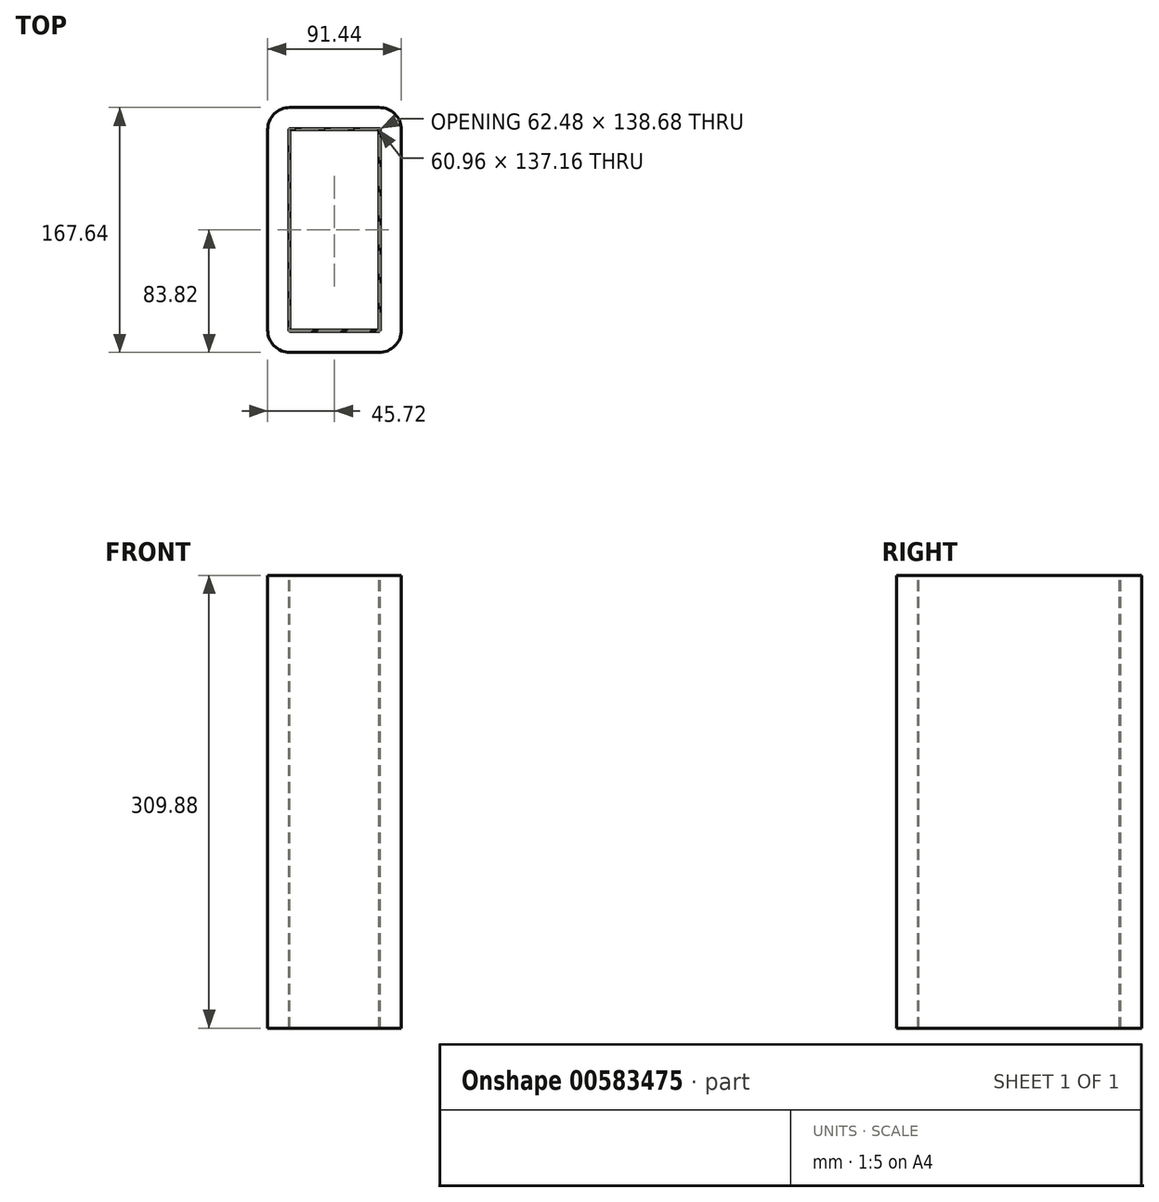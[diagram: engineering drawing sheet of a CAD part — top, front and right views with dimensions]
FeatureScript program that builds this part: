
annotation { "Feature Type Name" : "Feature", "Feature Type Description" : "" }
export const myFeature = defineFeature(function(context is Context, id is Id, definition is map)
    precondition{}
    {
        {
            assignVariable(context, id + "F0", {"name" : "Tongue", "anyValue" : 60.96 * mm});
        }
        {
            assignVariable(context, id + "F1", {"variableType" : VariableType.LENGTH, "name" : "CoreLength", "lengthValue" : 431.8 * mm});
        }
        {
            assignVariable(context, id + "F2", {"name" : "WindingWidth", "anyValue" : getVariable(context, 'CoreLength') - 2 * getVariable(context, 'Tongue')});
        }
        {
            assignVariable(context, id + "F3", {"name" : "CoilForm", "anyValue" : 0.76 * mm});
        }
        {
            assignVariable(context, id + "F4", {"name" : "CoilBuild", "anyValue" : 0.25 * getVariable(context, 'Tongue')});
        }
        {
            var Q0;
            Q0=qCreatedBy(makeId("Top.planeOp"),FACE);
            var sketch = newSketch(context, id + "F5", { "sketchPlane" : qUnion([Q0])});
            skLineSegment(sketch, "E0.bottom", {"start": v(-45.72, -83.82) * mm, "end": v(45.72, -83.82) * mm});
            skLineSegment(sketch, "E0.top", {"start": v(-45.72, 83.82) * mm, "end": v(45.72, 83.82) * mm});
            skLineSegment(sketch, "E0.left", {"start": v(-45.72, -83.82) * mm, "end": v(-45.72, 83.82) * mm});
            skLineSegment(sketch, "E0.right", {"start": v(45.72, -83.82) * mm, "end": v(45.72, 83.82) * mm});
            skPoint(sketch, "E0.middle", {"position": v(0, 0) * mm});
            skSolve(sketch);
        }
        {
            var Q0;
            Q0=qSketchRegion(id+"F5",true);
            extrude(context, id + "F6", {"entities" : qUnion([Q0]), "oppositeDirection" : true, "depth" : getVariable(context, 'WindingWidth')});
        }
        {
            var Q0;
            Q0=makeQuery(id+"F6.opExtrude","SWEPT_EDGE",EDGE,{"disambiguationData":[OSD([sQuery(id+"F5.wireOp",EDGE,"E0.top"),sQuery(id+"F5.wireOp",EDGE,"E0.left")])]});
            var Q1;
            Q1=makeQuery(id+"F6.opExtrude","SWEPT_EDGE",EDGE,{"disambiguationData":[OSD([sQuery(id+"F5.wireOp",EDGE,"E0.top"),sQuery(id+"F5.wireOp",EDGE,"E0.right")])]});
            var Q2;
            Q2=makeQuery(id+"F6.opExtrude","SWEPT_EDGE",EDGE,{"disambiguationData":[OSD([sQuery(id+"F5.wireOp",EDGE,"E0.bottom"),sQuery(id+"F5.wireOp",EDGE,"E0.right")])]});
            var Q3;
            Q3=makeQuery(id+"F6.opExtrude","SWEPT_EDGE",EDGE,{"disambiguationData":[OSD([sQuery(id+"F5.wireOp",EDGE,"E0.bottom"),sQuery(id+"F5.wireOp",EDGE,"E0.left")])]});
            fillet(context, id + "F7", {"entities" : qUnion([Q0, Q1, Q2, Q3]), "radius" : getVariable(context, 'CoilBuild'), "tangentPropagation" : true, "allowEdgeOverflow" : false});
        }
        {
            var Q0;
            Q0=makeQuery(id+"F6.opExtrude","CAP_FACE",FACE,{"disambiguationData":[OSD([sQuery(id+"F5.wireOp",EDGE,"E0.bottom"),sQuery(id+"F5.wireOp",EDGE,"E0.top"),sQuery(id+"F5.wireOp",EDGE,"E0.left"),sQuery(id+"F5.wireOp",EDGE,"E0.right")])],"isStart":true});
            var sketch = newSketch(context, id + "F8", { "sketchPlane" : qUnion([Q0])});
            skLineSegment(sketch, "E1.bottom", {"start": v(-31.24, -69.34) * mm, "end": v(31.24, -69.34) * mm});
            skLineSegment(sketch, "E1.top", {"start": v(-31.24, 69.34) * mm, "end": v(31.24, 69.34) * mm});
            skLineSegment(sketch, "E1.left", {"start": v(-31.24, -69.34) * mm, "end": v(-31.24, 69.34) * mm});
            skLineSegment(sketch, "E1.right", {"start": v(31.24, -69.34) * mm, "end": v(31.24, 69.34) * mm});
            skPoint(sketch, "E1.middle", {"position": v(0, 0) * mm});
            skSolve(sketch);
        }
        {
            var Q0;
            Q0=qSketchRegion(id+"F8",true);
            extrude(context, id + "F9", {"entities" : qUnion([Q0]), "operationType" : NewBodyOperationType.REMOVE, "oppositeDirection" : true, "depth" : getVariable(context, 'WindingWidth')});
        }
        {
            var Q0;
            Q0=makeQuery(id+"F6.opExtrude","CAP_FACE",FACE,{"disambiguationData":[OSD([sQuery(id+"F5.wireOp",EDGE,"E0.bottom"),sQuery(id+"F5.wireOp",EDGE,"E0.top"),sQuery(id+"F5.wireOp",EDGE,"E0.left"),sQuery(id+"F5.wireOp",EDGE,"E0.right")])],"isStart":true});
            var sketch = newSketch(context, id + "F10", { "sketchPlane" : qUnion([Q0])});
            skLineSegment(sketch, "E2.bottom", {"start": v(-31.24, -69.34) * mm, "end": v(31.24, -69.34) * mm});
            skLineSegment(sketch, "E2.top", {"start": v(-31.24, 69.34) * mm, "end": v(31.24, 69.34) * mm});
            skLineSegment(sketch, "E2.left", {"start": v(-31.24, -69.34) * mm, "end": v(-31.24, 69.34) * mm});
            skLineSegment(sketch, "E2.right", {"start": v(31.24, -69.34) * mm, "end": v(31.24, 69.34) * mm});
            skPoint(sketch, "E2.middle", {"position": v(0, 0) * mm});
            skSolve(sketch);
        }
        {
            var Q0;
            Q0=qSketchRegion(id+"F10",true);
            extrude(context, id + "F11", {"entities" : qUnion([Q0]), "oppositeDirection" : true, "depth" : getVariable(context, 'WindingWidth')});
        }
        {
            var Q0;
            Q0=makeQuery(id+"F11.opExtrude","CAP_FACE",FACE,{"disambiguationData":[OSD([sQuery(id+"F10.wireOp",EDGE,"E2.bottom"),sQuery(id+"F10.wireOp",EDGE,"E2.top"),sQuery(id+"F10.wireOp",EDGE,"E2.left"),sQuery(id+"F10.wireOp",EDGE,"E2.right")])],"isStart":true});
            var sketch = newSketch(context, id + "F12", { "sketchPlane" : qUnion([Q0])});
            skLineSegment(sketch, "E3.bottom", {"start": v(-30.48, 68.58) * mm, "end": v(30.48, 68.58) * mm});
            skLineSegment(sketch, "E3.top", {"start": v(-30.48, -68.58) * mm, "end": v(30.48, -68.58) * mm});
            skLineSegment(sketch, "E3.left", {"start": v(-30.48, 68.58) * mm, "end": v(-30.48, -68.58) * mm});
            skLineSegment(sketch, "E3.right", {"start": v(30.48, 68.58) * mm, "end": v(30.48, -68.58) * mm});
            skPoint(sketch, "E3.middle", {"position": v(0, 0) * mm});
            skSolve(sketch);
        }
        {
            var Q0;
            Q0=qSketchRegion(id+"F12",true);
            extrude(context, id + "F13", {"entities" : qUnion([Q0]), "operationType" : NewBodyOperationType.REMOVE, "oppositeDirection" : true, "depth" : getVariable(context, 'WindingWidth')});
        }
        {
            var Q0;
            Q0=makeQuery(id+"F11.opExtrude","SWEPT_EDGE",EDGE,{"disambiguationData":[OSD([sQuery(id+"F10.wireOp",EDGE,"E2.top"),sQuery(id+"F10.wireOp",EDGE,"E2.left")])]});
            var Q1;
            Q1=makeQuery(id+"F11.opExtrude","SWEPT_EDGE",EDGE,{"disambiguationData":[OSD([sQuery(id+"F10.wireOp",EDGE,"E2.top"),sQuery(id+"F10.wireOp",EDGE,"E2.right")])]});
            var Q2;
            Q2=makeQuery(id+"F11.opExtrude","SWEPT_EDGE",EDGE,{"disambiguationData":[OSD([sQuery(id+"F10.wireOp",EDGE,"E2.bottom"),sQuery(id+"F10.wireOp",EDGE,"E2.right")])]});
            var Q3;
            Q3=makeQuery(id+"F11.opExtrude","SWEPT_EDGE",EDGE,{"disambiguationData":[OSD([sQuery(id+"F10.wireOp",EDGE,"E2.bottom"),sQuery(id+"F10.wireOp",EDGE,"E2.left")])]});
            fillet(context, id + "F14", {"entities" : qUnion([Q0, Q1, Q2, Q3]), "radius" : getVariable(context, 'CoilForm'), "tangentPropagation" : true, "allowEdgeOverflow" : false});
        }
        {
            var Q0;
            Q0=makeQuery(id+"F9.boolean.opBoolean","COPY",EDGE,{"derivedFrom":makeQuery(id+"F9.opExtrude","SWEPT_EDGE",EDGE,{"disambiguationData":[OSD([sQuery(id+"F8.wireOp",EDGE,"E1.top"),sQuery(id+"F8.wireOp",EDGE,"E1.left")])]})});
            var Q1;
            Q1=makeQuery(id+"F9.boolean.opBoolean","COPY",EDGE,{"derivedFrom":makeQuery(id+"F9.opExtrude","SWEPT_EDGE",EDGE,{"disambiguationData":[OSD([sQuery(id+"F8.wireOp",EDGE,"E1.bottom"),sQuery(id+"F8.wireOp",EDGE,"E1.left")])]})});
            var Q2;
            Q2=makeQuery(id+"F9.boolean.opBoolean","COPY",EDGE,{"derivedFrom":makeQuery(id+"F9.opExtrude","SWEPT_EDGE",EDGE,{"disambiguationData":[OSD([sQuery(id+"F8.wireOp",EDGE,"E1.bottom"),sQuery(id+"F8.wireOp",EDGE,"E1.right")])]})});
            var Q3;
            Q3=makeQuery(id+"F9.boolean.opBoolean","COPY",EDGE,{"derivedFrom":makeQuery(id+"F9.opExtrude","SWEPT_EDGE",EDGE,{"disambiguationData":[OSD([sQuery(id+"F8.wireOp",EDGE,"E1.top"),sQuery(id+"F8.wireOp",EDGE,"E1.right")])]})});
            fillet(context, id + "F15", {"entities" : qUnion([Q0, Q1, Q2, Q3]), "radius" : getVariable(context, 'CoilForm'), "tangentPropagation" : true, "allowEdgeOverflow" : false});
        }
    });
